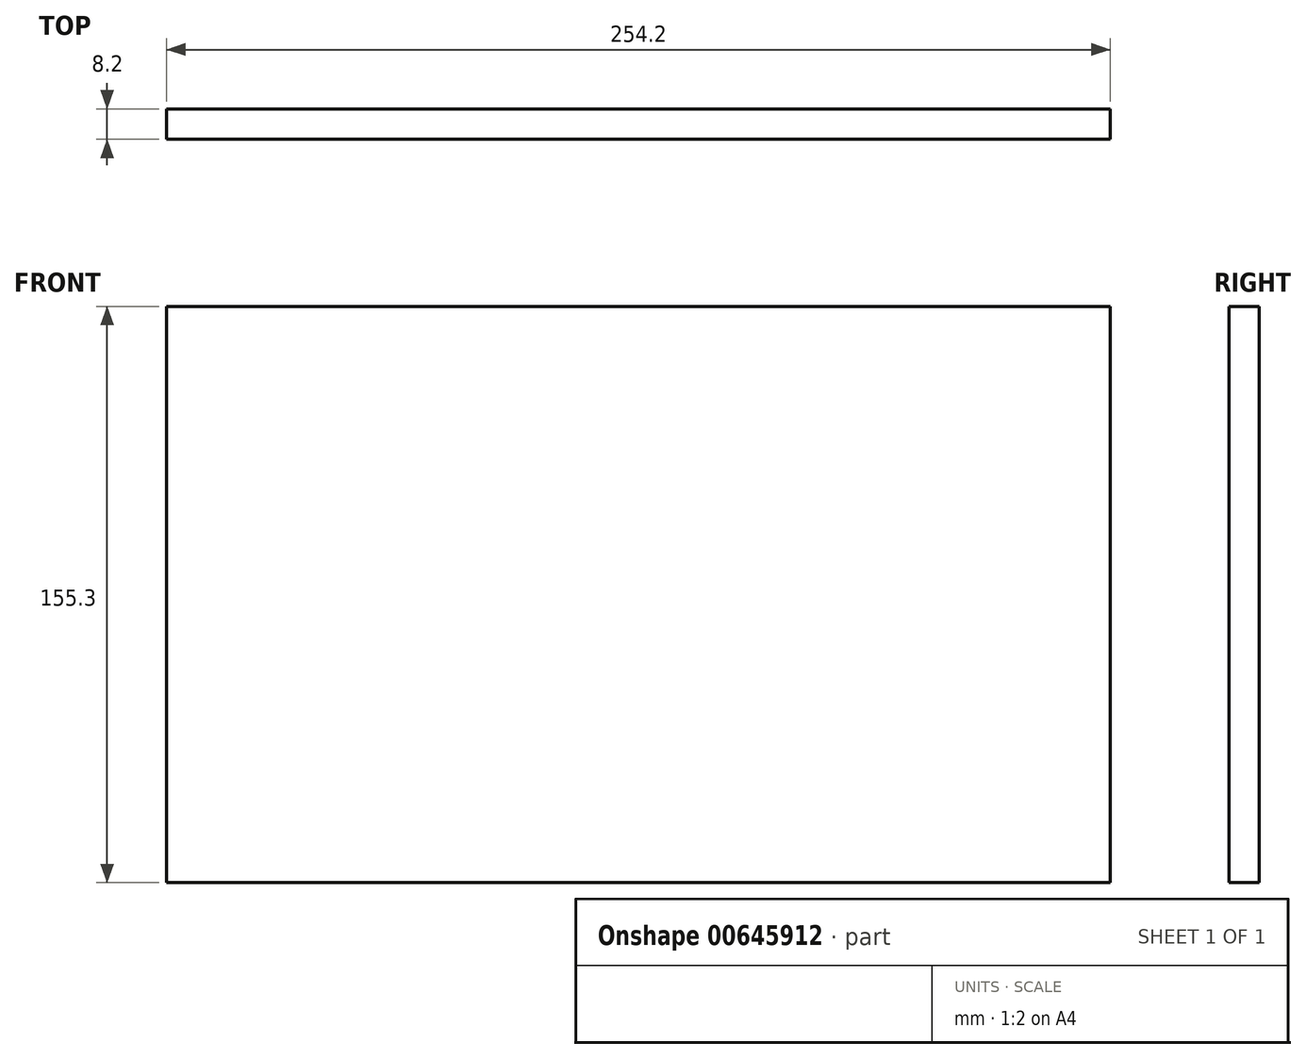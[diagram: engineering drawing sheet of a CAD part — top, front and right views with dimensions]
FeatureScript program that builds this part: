
annotation { "Feature Type Name" : "Feature", "Feature Type Description" : "" }
export const myFeature = defineFeature(function(context is Context, id is Id, definition is map)
    precondition{}
    {
        {
            var Q0;
            Q0=qCreatedBy(makeId("Front.planeOp"), FACE);
            var sketch = newSketch(context, id + "F0", { "sketchPlane" : qUnion([Q0])});
            skLineSegment(sketch, "E0.bottom", {"start": v(258.37, 0) * mm, "end": v(4.17, 0) * mm});
            skLineSegment(sketch, "E0.top", {"start": v(258.37, 155.3) * mm, "end": v(4.17, 155.3) * mm});
            skLineSegment(sketch, "E0.left", {"start": v(258.37, 0) * mm, "end": v(258.37, 155.3) * mm});
            skLineSegment(sketch, "E0.right", {"start": v(4.17, 0) * mm, "end": v(4.17, 155.3) * mm});
            skPoint(sketch, "E0.middle", {"position": v(131.27, 77.65) * mm});
            skSolve(sketch);
        }
        {
            var Q0;
            Q0 = qSketchRegion(id + "F0", true);
            extrude(context, id + "F1", {"entities" : qUnion([Q0]), "depth" : 8.2 * mm, "offsetDistance" : 25 * mm});
        }
    });
